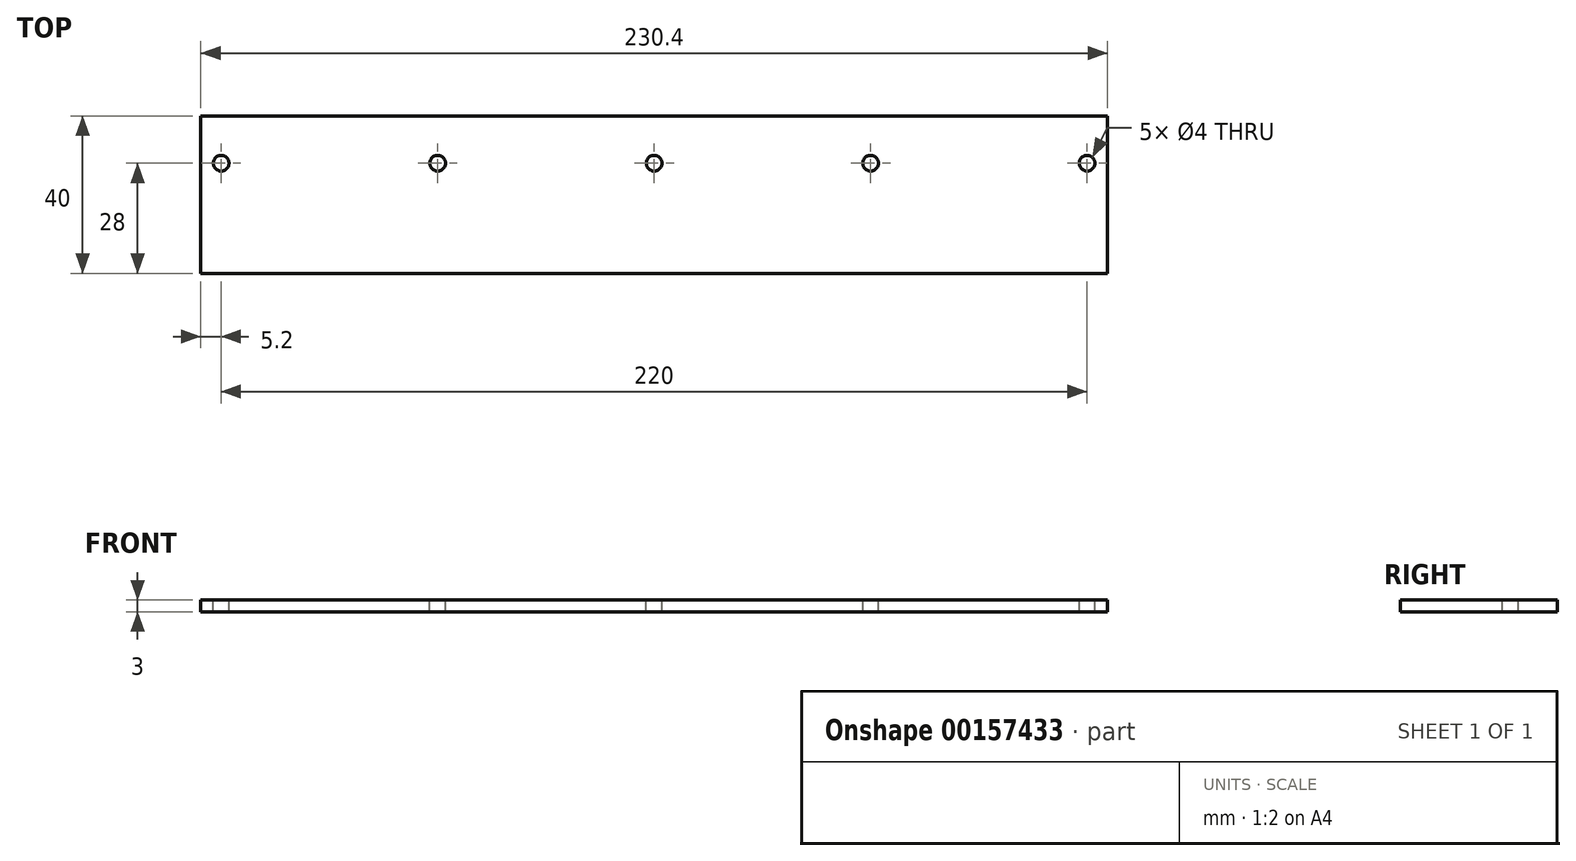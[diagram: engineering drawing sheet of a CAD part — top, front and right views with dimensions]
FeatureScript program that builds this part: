
annotation { "Feature Type Name" : "Feature", "Feature Type Description" : "" }
export const myFeature = defineFeature(function(context is Context, id is Id, definition is map)
    precondition{}
    {
        {
            var Q0;
            Q0=qCreatedBy(makeId("Top.planeOp"),FACE);
            var sketch = newSketch(context, id + "F0", { "sketchPlane" : qUnion([Q0])});
            skLineSegment(sketch, "E0.bottom", {"start": v(0, 0) * mm, "end": v(230.4, 0) * mm});
            skLineSegment(sketch, "E0.top", {"start": v(0, 40) * mm, "end": v(230.4, 40) * mm});
            skLineSegment(sketch, "E0.left", {"start": v(0, 0) * mm, "end": v(0, 40) * mm});
            skLineSegment(sketch, "E0.right", {"start": v(230.4, 0) * mm, "end": v(230.4, 40) * mm});
            skSolve(sketch);
        }
        {
            var Q0;
            Q0 = qSketchRegion(id + "F0", true);
            extrude(context, id + "F1", {"entities" : qUnion([Q0]), "depth" : 3 * mm});
        }
        {
            var Q0;
            Q0=makeQuery(id+"F1.opExtrude","CAP_FACE",FACE,{"disambiguationData":[OSD([sQuery(id+"F0.wireOp",EDGE,"E0.bottom"),sQuery(id+"F0.wireOp",EDGE,"E0.top"),sQuery(id+"F0.wireOp",EDGE,"E0.left"),sQuery(id+"F0.wireOp",EDGE,"E0.right")])],"isStart":false});
            var sketch = newSketch(context, id + "F2", { "sketchPlane" : qUnion([Q0])});
            skCircle(sketch, "E1", {"center": v(5.2, 28) * mm, "radius": 2 * mm});
            skCircle(sketch, "E2.1.0.0", {"center": v(60.2, 28) * mm, "radius": 2 * mm});
            skCircle(sketch, "E2.2.0.0", {"center": v(115.2, 28) * mm, "radius": 2 * mm});
            skCircle(sketch, "E2.3.0.0", {"center": v(170.2, 28) * mm, "radius": 2 * mm});
            skCircle(sketch, "E2.4.0.0", {"center": v(225.2, 28) * mm, "radius": 2 * mm});
            skLineSegment(sketch, "E2.direction1", {"start": v(5.2, 28) * mm, "end": v(60.2, 28) * mm, "construction": true});
            skSolve(sketch);
        }
        {
            var Q0;
            Q0 = qSketchRegion(id + "F2", true);
            extrude(context, id + "F3", {"entities" : qUnion([Q0]), "operationType" : NewBodyOperationType.REMOVE, "endBound" : BoundingType.THROUGH_ALL, "oppositeDirection" : true, "depth" : 25 * mm});
        }
    });
